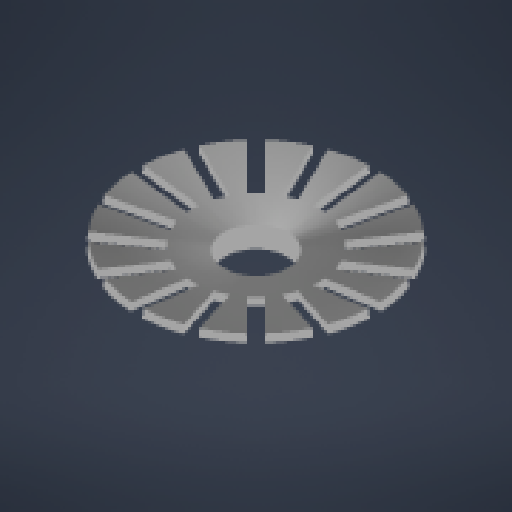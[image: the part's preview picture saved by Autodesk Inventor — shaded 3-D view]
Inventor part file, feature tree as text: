
AUTODESK INVENTOR PART (.ipt)
format: ipt  version: 2024 (Build 280153000, 153)  size: 379,904 bytes
history: native  units: mm
features: sketch x5, extrude x4, plane x2, fillet x2, other x2, revolve x1, pattern_circular x1
ambient origin geometry x8: Origin, YZ Plane, XZ Plane, XY Plane, X Axis, Y Axis, Z Axis, Center Point
bodies: Solid1 (feature_tree)
feature tree (17):
  revolve  "Revolution1"  [1 undecoded]
  plane  "Work Plane1"
  extrude  "Extrusion1"  Depth=4.0mm
  pattern_circular  "Circular Pattern1"  [2 undecoded]
  plane  "Work Plane2"
  extrude  "Extrusion2"  Depth=10.0mm TaperAngle=360.0deg
  fillet  "Fillet1"  [1 undecoded]
  extrude  "Extrusion3"  Depth=8.0mm
  fillet  "Fillet6"  Radius=1.5mm
  extrude  "Extrusión19"  Depth=10.0mm
  other  "Edición directa1"
  sketch  "Sketch1"  dims[d2=1.0mm d3=2.5mm]
  sketch  "Sketch2"  dims[d4=90.0deg d5=4.0mm]
  sketch  "Sketch3"  dims[d6=16.0mm]
  sketch  "Sketch4"  dims[d7=0.75mm]
  sketch  "Boceto21"  dims[d8=0.75mm d9=10.0mm d10=0.0mm d11=160.0mm d12=360.0deg d14=-0.7mm d15=8.0mm d16=1.5mm d17=0.0mm d18=0.5mm d19=8.0mm d20=4.0mm d21=0.0mm d42=2.0mm d83=100.0mm d84=0.0mm d85=40.0mm d86=10.0mm d87=10.0mm]
  other  "Escala1"
note: 4 required parameter values undecoded (feature->parameter linkage not recoverable at this tier; creation-order binding heuristic only, values carry confidence <= 0.55)